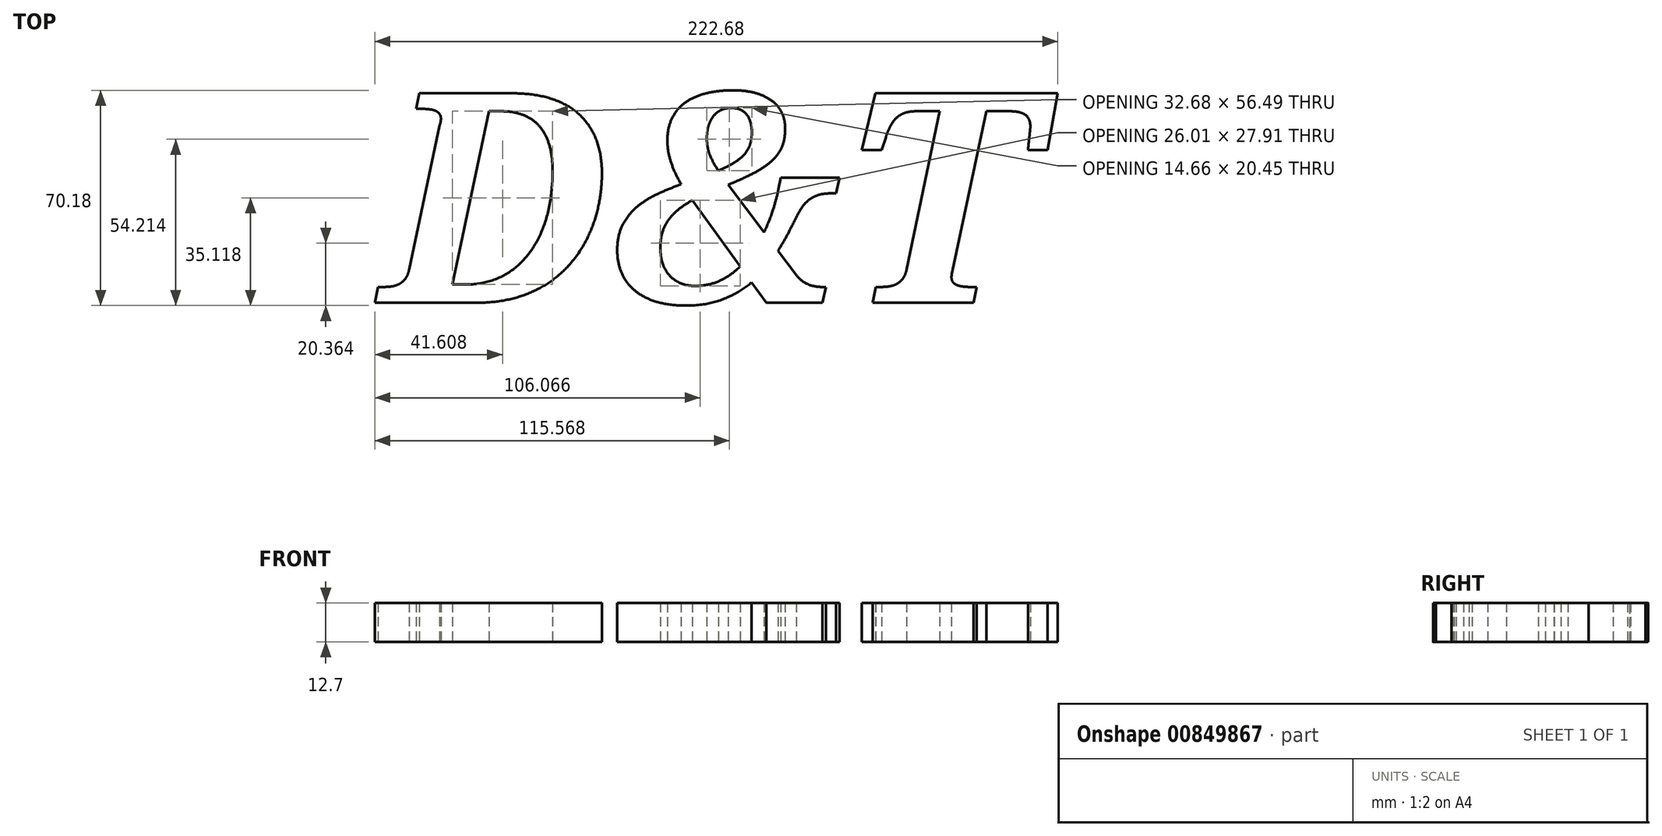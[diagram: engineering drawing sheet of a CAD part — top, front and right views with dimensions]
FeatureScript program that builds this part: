
annotation { "Feature Type Name" : "Feature", "Feature Type Description" : "" }
export const myFeature = defineFeature(function(context is Context, id is Id, definition is map)
    precondition{}
    {
        {
            var Q0;
            Q0=qCreatedBy(makeId("Top.planeOp"),FACE);
            var sketch = newSketch(context, id + "F0", { "sketchPlane" : qUnion([Q0])});
            skText(sketch, "E0", { "text": "D&T", "fontName": "NotoSerif-BoldItalic.ttf"});
            const initialGuessF0  = {"E0": [-0.22887, -0.06885, 1, 0, 0.06885]};
            skSetInitialGuess(sketch, initialGuessF0);
            skSolve(sketch);
        }
        {
            var Q0;
            Q0 = qSketchRegion(id + "F0", true);
            extrude(context, id + "F1", {"entities" : qUnion([Q0]), "depth" : 12.7 * mm, "offsetDistance" : 25.4 * mm});
        }
    });
